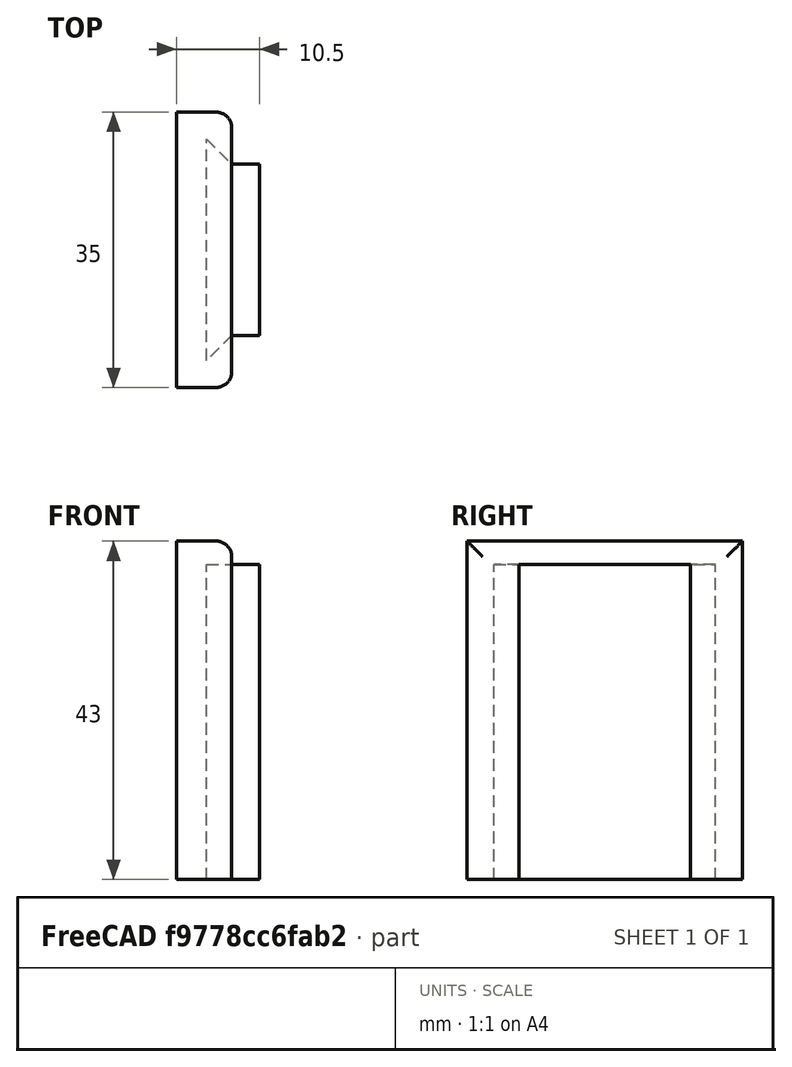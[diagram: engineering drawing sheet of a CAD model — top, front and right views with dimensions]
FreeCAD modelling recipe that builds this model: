
FCSTD DOCUMENT  (FreeCAD 0.20R29603 (Git))
Label: Remote Holder
License: All rights reserved
LicenseURL: http://en.wikipedia.org/wiki/All_rights_reserved
objects: Sketcher::SketchObject×4, PartDesign::Body×3, PartDesign::Pad×3, PartDesign::ShapeBinder×2, Image::ImagePlane×1, PartDesign::Fillet×1
note: 17 computed .brp shape members not serialized (recipe doc carries the construction recipe); baked Part::Feature solids carry a one-line shape summary decoded from their .brp

FEATURE [Image::ImagePlane] ImagePlane
  XSize = 113.118
  YSize = 84.8385
FEATURE [Sketcher::SketchObject] Sketch  label="Image Sketch"
  FullyConstrained = true
  MapMode = 5
  Support = -> [XY_Plane]
  sketch-geometry (2):
    g0: ArcOfCircle CenterX=60.52 CenterY=4.4e-15 CenterZ=0 NormalX=0 NormalY=0 NormalZ=1 AngleXU=0 Radius=63.1916 StartAngle=2.84977 EndAngle=3.43341
    g1: LineSegment StartX=0 StartY=-18.18 StartZ=0 EndX=0 EndY=18.18 EndZ=0
  constraints (6):
    c: Coincident(g1,g0)
    c: Coincident(g1,g0)
    c: Vertical(g1)
    c: DistanceY(g1,g1) = 36.36
    c: Symmetric(g0,g0,g-1)
    c: DistanceX(g-1,g0) = 60.52
FEATURE [PartDesign::Body] Body  label="Reference"
  Group = -> [Sketch]
  Origin = -> Origin
FEATURE [PartDesign::ShapeBinder] ShapeBinder  label="Bind Reference"
  Support = -> [Sketch]
  TraceSupport = false
FEATURE [Sketcher::SketchObject] Sketch001
  ExternalGeometry = -> [ShapeBinder]
  FullyConstrained = true
  MapMode = 5
  Support = -> [XY_Plane001]
  sketch-geometry (13):
    g0: GeomPoint X=-1.73094 Y=10.863 Z=0
    g1: GeomPoint X=-1.73094 Y=-10.863 Z=0
    g2: ArcOfCircle CenterX=60.52 CenterY=3.6e-15 CenterZ=0 NormalX=0 NormalY=0 NormalZ=1 AngleXU=0 Radius=63.1916 StartAngle=2.96883 EndAngle=3.31436
    g3: LineSegment StartX=-1.73094 StartY=10.863 StartZ=0 EndX=60.52 EndY=3.6e-15 EndZ=0
    g4: LineSegment StartX=-1.73094 StartY=-10.863 StartZ=0 EndX=60.52 EndY=3.6e-15 EndZ=0
    g5: LineSegment StartX=-1.73094 StartY=-10.863 StartZ=0 EndX=0 EndY=0 EndZ=0
    g6: LineSegment StartX=0 StartY=0 StartZ=0 EndX=-1.73094 EndY=10.863 EndZ=0
    g7: LineSegment StartX=-1.73094 StartY=10.863 StartZ=0 EndX=-5.23094 EndY=10.863 EndZ=0
    g8: LineSegment StartX=-5.23094 StartY=10.863 StartZ=0 EndX=-8.41292 EndY=14.0449 EndZ=0
    g9: LineSegment StartX=-8.41292 StartY=14.0449 StartZ=0 EndX=-8.41292 EndY=-14.0449 EndZ=0
    g10: LineSegment StartX=-8.41292 StartY=-14.0449 StartZ=0 EndX=-5.23094 EndY=-10.863 EndZ=0
    g11: LineSegment StartX=-5.23094 StartY=-10.863 StartZ=0 EndX=-1.73094 EndY=-10.863 EndZ=0
    g12: LineSegment StartX=-1.73094 StartY=-10.863 StartZ=0 EndX=-1.73094 EndY=10.863 EndZ=0
  constraints (30):
    c: PointOnObject(g0,g-3)
    c: Coincident(g2,g-3)
    c: Coincident(g2,g1)
    c: Coincident(g2,g0)
    c: Coincident(g3,g2)
    c: Coincident(g3,g2)
    c: Coincident(g4,g2)
    c: Coincident(g4,g2)
    c: Coincident(g5,g2)
    c: Coincident(g5,g-1)
    c: Coincident(g6,g5)
    c: Coincident(g6,g2)
    c: Equal(g6,g5)
    c: Coincident(g2,g7)
    c: Coincident(g7,g8)
    c: Coincident(g8,g9)
    c: Vertical(g9)
    c: Coincident(g9,g10)
    c: Coincident(g10,g11)
    c: Coincident(g2,g11)
    c: Horizontal(g7)
    c: Horizontal(g11)
    c: Equal(g11,g7)
    c: Angle(g10,g11) = 2.35619
    c: Angle(g7,g8) = 2.35619
    c: Distance(g6) = 11
    c: DistanceX(g7,g7) = 3.5
    c: Distance(g8) = 4.5
    c: Coincident(g12,g11)
    c: Coincident(g12,g7)
FEATURE [PartDesign::Pad] Pad
  Direction = (0,0,1)
  Length = 40
  Length2 = 10
  Profile = -> Sketch001
  ReferenceAxis = -> Sketch001 [N_Axis]
  Refine = true
  Type = 0
FEATURE [PartDesign::Body] Body001  label="Remote Clip"
  Group = -> [ShapeBinder,Sketch001,Pad]
  Origin = -> Origin001
  Tip = -> Pad
FEATURE [PartDesign::ShapeBinder] ShapeBinder001  label="Bind Clip"
  Support = -> [Pad]
  TraceSupport = false
FEATURE [Sketcher::SketchObject] Sketch002
  ExternalGeometry = -> [ShapeBinder001]
  FullyConstrained = true
  MapMode = 5
  Placement = pos=(0,0,0) rot=(1,0,0;3.14159rad)
  Support = -> [ShapeBinder001]
  sketch-geometry (8):
    g0: LineSegment StartX=-8.41292 StartY=14.0449 StartZ=0 EndX=-8.41292 EndY=-14.0449 EndZ=0
    g1: LineSegment StartX=-8.41292 StartY=-14.0449 StartZ=0 EndX=-1.73094 EndY=10.863 EndZ=0
    g2: LineSegment StartX=-1.73094 StartY=10.863 StartZ=0 EndX=-5.23094 EndY=10.863 EndZ=0
    g3: LineSegment StartX=-8.41292 StartY=14.0449 StartZ=0 EndX=-8.41292 EndY=29.9539 EndZ=0
    g4: LineSegment StartX=-8.41292 StartY=29.9539 StartZ=0 EndX=-15.4129 EndY=29.9539 EndZ=0
    g5: LineSegment StartX=-15.4129 StartY=29.9539 StartZ=0 EndX=-15.4129 EndY=-5.04605 EndZ=0
    g6: LineSegment StartX=-15.4129 StartY=-5.04605 StartZ=0 EndX=-5.23094 EndY=-5.04605 EndZ=0
    g7: LineSegment StartX=-5.23094 StartY=-5.04605 StartZ=0 EndX=-5.23094 EndY=10.863 EndZ=0
  constraints (20):
    c: Coincident(g0,g-4)
    c: Coincident(g0,g-4)
    c: Coincident(g1,g0)
    c: Coincident(g1,g-5)
    c: Coincident(g2,g1)
    c: Coincident(g2,g-5)
    c: Coincident(g0,g3)
    c: Vertical(g3)
    c: Coincident(g3,g4)
    c: Horizontal(g4)
    c: Coincident(g4,g5)
    c: Vertical(g5)
    c: Coincident(g5,g6)
    c: Horizontal(g6)
    c: Coincident(g6,g7)
    c: Coincident(g7,g2)
    c: Vertical(g7)
    c: Equal(g3,g7)
    c: DistanceX(g4,g4) = 7
    c: DistanceY(g5,g5) = 35
FEATURE [PartDesign::Pad] Pad001
  Direction = (0,0,-1)
  Length = 40
  Length2 = 10
  Profile = -> Sketch002
  ReferenceAxis = -> Sketch002 [N_Axis]
  Refine = true
  Reversed = true
  Type = 0
FEATURE [Sketcher::SketchObject] Sketch003
  ExternalGeometry = -> [Pad001]
  FullyConstrained = true
  MapMode = 5
  Placement = pos=(0,0,40) rot=(0,0,1;0rad)
  Support = -> [Pad001]
  sketch-geometry (4):
    g0: LineSegment StartX=-12.2309 StartY=17.5 StartZ=0 EndX=-5.23094 EndY=17.5 EndZ=0
    g1: LineSegment StartX=-5.23094 StartY=17.5 StartZ=0 EndX=-5.23094 EndY=-17.5 EndZ=0
    g2: LineSegment StartX=-5.23094 StartY=-17.5 StartZ=0 EndX=-12.2309 EndY=-17.5 EndZ=0
    g3: LineSegment StartX=-12.2309 StartY=-17.5 StartZ=0 EndX=-12.2309 EndY=17.5 EndZ=0
  constraints (10):
    c: Coincident(g0,g1)
    c: Coincident(g1,g2)
    c: Coincident(g2,g3)
    c: Coincident(g3,g0)
    c: Horizontal(g0)
    c: Horizontal(g2)
    c: Vertical(g1)
    c: Vertical(g3)
    c: Coincident(g0,g-4)
    c: Coincident(g1,g-5)
FEATURE [PartDesign::Pad] Pad002
  BaseFeature = -> Pad001
  Direction = (0,0,1)
  Length = 3
  Length2 = 10
  Profile = -> Sketch003
  ReferenceAxis = -> Sketch003 [N_Axis]
  Refine = true
  Type = 0
FEATURE [PartDesign::Fillet] Fillet
  Base = -> Pad002 [Edge19,Edge17,Edge18]
  BaseFeature = -> Pad002
  Radius = 2
  Refine = true
  SupportTransform = false
  UseAllEdges = false
FEATURE [PartDesign::Body] Body002  label="Wall Clip"
  Group = -> [ShapeBinder001,Sketch002,Pad001,Sketch003,Pad002,Fillet]
  Origin = -> Origin002
  Tip = -> Fillet
